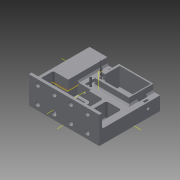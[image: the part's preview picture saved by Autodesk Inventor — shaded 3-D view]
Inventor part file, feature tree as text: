
AUTODESK INVENTOR PART (.ipt)
format: ipt  version: 2015 (Build 190159000, 159)  size: 758,272 bytes
history: native  units: in
note: dims shown in document units (in); Inventor stores cm internally (conversion verified against a paired STEP export)
features: sketch x31, extrude x28, chamfer x12, other x4, revolve x2, plane x1
ambient origin geometry x8: Origin, YZ Plane, XZ Plane, XY Plane, X Axis, Y Axis, Z Axis, Center Point
bodies: Solid1 (feature_tree)
feature tree (78):
  extrude  "Extrusion1"  Depth=3.4961in
  extrude  "Extrusion3"  TaperAngle=0.0deg  [1 undecoded]
  extrude  "Extrusion4"  Depth=1.0315in
  extrude  "Extrusion5"  Depth=1.5276in
  extrude  "Extrusion6"  Depth=0.1181in
  extrude  "Extrusion7"  TaperAngle=0.0deg  [1 undecoded]
  extrude  "Extrusion8"  TaperAngle=0.0deg  [1 undecoded]
  extrude  "Extrusion9"  TaperAngle=0.0deg  [1 undecoded]
  extrude  "Extrusion10"  Depth=0.1181in
  extrude  "Extrusion11"  Depth=0.1969in
  extrude  "Extrusion12"  Depth=0.437in
  plane  "Work Plane2"
  sketch  "Sketch25"  dims[d29=1.2126in d30=1.378in d31=0.0in]
  other  "Work Axis5"
  other  "Work Axis6"
  extrude  "Extrusion13"  Depth=1.378in TaperAngle=0.0deg
  extrude  "Extrusion14"  TaperAngle=0.0deg  [1 undecoded]
  extrude  "Extrusion15"  TaperAngle=0.0deg  [1 undecoded]
  extrude  "Extrusion16"  TaperAngle=0.0deg  [1 undecoded]
  extrude  "Extrusion17"  TaperAngle=0.0deg  [1 undecoded]
  extrude  "Extrusion18"  TaperAngle=0.0deg  [1 undecoded]
  other  "Work Axis7"
  other  "Work Axis8"
  extrude  "Extrusion19"  TaperAngle=0.0deg  [1 undecoded]
  extrude  "Extrusion20"  Depth=0.0787in TaperAngle=0.0deg
  revolve  "Revolution4"  [1 undecoded]
  chamfer  "Chamfer1"  Distance=0.0787in
  extrude  "Extrusion23"  Depth=0.1575in
  extrude  "Extrusion24"  Depth=0.1575in
  extrude  "Extrusion25"  Depth=0.1575in
  extrude  "Extrusion26"  Depth=0.3858in
  chamfer  "Chamfer2"  Distance=1.378in
  chamfer  "Chamfer3"  Distance=0.1181in
  chamfer  "Chamfer4"  Distance=0.315in
  extrude  "Extrusion27"  Depth=0.3031in
  chamfer  "Chamfer5"  Distance=0.1575in
  extrude  "Extrusion28"  Depth=0.315in
  sketch  "Sketch55"  dims[d67=0.3858in d68=1.378in d69=0.0in]
  chamfer  "Chamfer6"  Distance=0.1575in
  chamfer  "Chamfer7"  Distance=0.315in
  chamfer  "Chamfer8"  Distance=0.9252in
  extrude  "Extrusion29"  Depth=0.7874in TaperAngle=0.0deg
  chamfer  "Chamfer9"  [1 undecoded]
  chamfer  "Chamfer10"  [1 undecoded]
  extrude  "Extrusion30"  Depth=0.0787in
  extrude  "Extrusion31"  Depth=0.1575in
  chamfer  "Chamfer11"  Distance=0.6693in
  chamfer  "Chamfer12"  [1 undecoded]
  revolve  "Revolution5"  [1 undecoded]
  sketch  "Sketch63"  dims[d74=0.3071in d75=0.1181in d76=0.315in d77=0.0in d78=0.3031in d79=0.1575in d80=0.315in d81=0.1575in d82=0.315in d83=0.9252in d84=0.7874in d85=0.0in d86=0.0in d87=0.0in d89=0.0787in d91=0.1575in d92=0.6693in d93=0.0in d97=0.0in d98=0.0in d99=0.0in d100=0.0in d101=0.3937in d102=0.0in d105=-0.5118in d113=45.0deg d114=0.5118in d115=0.0689in d117=0.2264in d118=0.1969in d119=0.6102in d120=0.0in d121=0.1024in d122=0.0in d123=45.0deg d124=0.0591in d125=0.7087in d126=0.3307in d127=0.2795in d129=0.4331in d130=0.7087in d131=0.0in d132=0.0in d135=0.0591in d137=0.2598in d138=0.0512in d139=0.0512in d140=0.4823in d141=0.0in d145=0.7087in d146=0.0in d147=0.5118in d152=0.6102in d153=0.0in d154=0.2756in d155=0.4724in d156=0.2854in d157=0.2756in d158=0.9646in d159=0.2756in d160=0.9646in d161=0.2756in d162=0.9646in d163=0.2756in d164=0.9646in d166=0.2756in d167=0.9646in d169=0.2756in d170=0.9646in d171=0.2756in d172=0.9646in d173=0.9646in d174=0.1575in d175=0.2362in d176=0.0in d177=0.0in d194=0.9252in d195=1.0433in d196=0.1575in d197=0.315in d199=0.0787in d202=0.0787in d205=0.0787in d210=0.3937in d211=0.0in d213=0.0in d214=0.0in d216=0.1575in d217=0.0787in d218=0.0787in d219=0.1693in d220=0.0in d221=0.0in d222=90.0deg d227=1.0315in d236=0.0787in d237=0.0787in d238=45.0deg d239=0.0984in d241=1.811in d242=0.2165in d243=0.0in d244=0.0in d247=0.0591in d249=0.9646in d250=0.9646in d254=0.2264in d255=0.2854in d256=0.3937in d257=0.0in d258=0.0in d259=0.0in d260=0.0in d261=0.0in d262=0.0in d263=0.0in d264=0.0in d265=0.1575in d266=0.0354in d267=0.0in d268=0.6083in d269=0.3591in d270=0.3in d271=0.0in d272=0.0in d275=0.0in d276=0.0in d277=0.0in d278=0.1575in d279=0.3937in d280=0.0in d283=0.0in d284=0.0in d285=0.0in d286=0.1575in d287=0.3937in d288=0.0in d289=0.1181in d290=0.0in d293=0.0in d298=0.0in d300=0.0in d301=0.0787in d302=0.0787in d303=45.0deg d304=0.0787in d305=0.0787in d306=45.0deg d307=0.0787in d308=0.0787in d309=45.0deg d310=0.0in d311=0.0in d312=0.0in d313=0.0in d314=0.0in d315=0.0in d316=0.0in d318=0.0in d319=0.0in d320=0.2362in d321=0.0in d322=0.0787in d323=0.0787in d324=45.0deg d327=0.0787in d328=0.1181in d329=0.4724in d330=0.0in d331=0.1378in d332=0.0787in d333=0.0787in d334=45.0deg d335=0.0787in d336=0.0787in d337=45.0deg d338=0.0787in d339=0.0787in d340=45.0deg d341=0.0in d342=0.0in d343=0.1181in d344=0.0in d345=0.0in d346=0.0in d347=0.0in d348=0.1181in d349=0.0394in d352=0.0in d353=0.0in d354=0.0in d355=0.0394in d356=0.7087in d357=0.0in d358=0.0787in d359=0.0787in d360=45.0deg d361=0.0787in d362=0.0787in d363=45.0deg d364=0.0in d365=0.0in d366=0.0in d367=0.0in d368=0.0in d369=0.0in d370=0.0in d371=0.0in d372=0.0394in d373=0.0in d374=0.0394in d375=0.0in d376=0.0787in d377=0.0787in d378=45.0deg d379=0.0787in d380=0.0787in d381=45.0deg d383=0.0394in d386=1.7126in d387=0.0591in d393=90.0deg d394=0.0591in d398=0.0591in d399=0.0591in d400=0.3937in d401=0.3937in d402=0.0in d403=0.2559in d405=0.2854in d406=0.1575in]
  sketch  "Sketch1"  dims[d0=3.8583in d1=3.4961in]
  sketch  "Sketch3"  dims[d3=1.5748in d4=0.0in d9=0.0in]
  sketch  "Sketch4"  dims[d10=0.1575in d11=1.0315in]
  sketch  "Sketch5"  dims[d12=1.1024in d13=1.5276in]
  sketch  "Sketch6"  dims[d14=0.7717in d15=0.1181in]
  sketch  "Sketch7"  dims[d16=0.0in d17=0.0in]
  sketch  "Sketch8"  dims[d18=0.5906in d19=0.0in]
  sketch  "Sketch9"  dims[d20=0.0in d21=0.0in]
  sketch  "Sketch10"  dims[d22=0.1181in d23=0.1181in]
  sketch  "Sketch11"  dims[d24=0.8268in d25=0.1969in]
  sketch  "Sketch13"  dims[d26=0.1575in d28=0.437in]
  sketch  "Sketch28"  dims[d32=0.0in d33=0.0in]
  sketch  "Sketch31"  dims[d34=0.0in d35=0.0in]
  sketch  "Sketch33"  dims[d36=0.0in d37=0.0in]
  sketch  "Sketch34"  dims[d38=0.0in d39=0.0in]
  sketch  "Sketch35"  dims[d40=0.0in d41=0.0in]
  sketch  "Sketch36"  dims[d42=0.0in d43=0.0in]
  sketch  "Sketch37"  dims[d44=0.1969in d45=0.0in d50=0.0787in d51=0.0in]
  sketch  "Sketch38"  dims[d52=0.0in d53=0.0in]
  sketch  "Sketch42"  dims[d54=0.7874in]
  sketch  "Sketch43"  dims[d55=0.1575in d56=0.0787in d57=0.0in]
  sketch  "Sketch46"  dims[d58=0.1575in d59=0.1575in]
  sketch  "Sketch49"  dims[d60=0.1575in d61=0.1575in]
  sketch  "Sketch53"  dims[d62=0.1969in d63=0.0in d64=0.1575in]
  sketch  "Sketch54"  dims[d65=0.1969in d66=0.3858in]
  sketch  "Sketch56"  dims[d71=0.2362in]
  sketch  "Sketch57"  dims[d72=0.3071in]
  sketch  "Sketch62"  dims[d73=0.1575in]
note: 15 required parameter values undecoded (feature->parameter linkage not recoverable at this tier; creation-order binding heuristic only, values carry confidence <= 0.55)